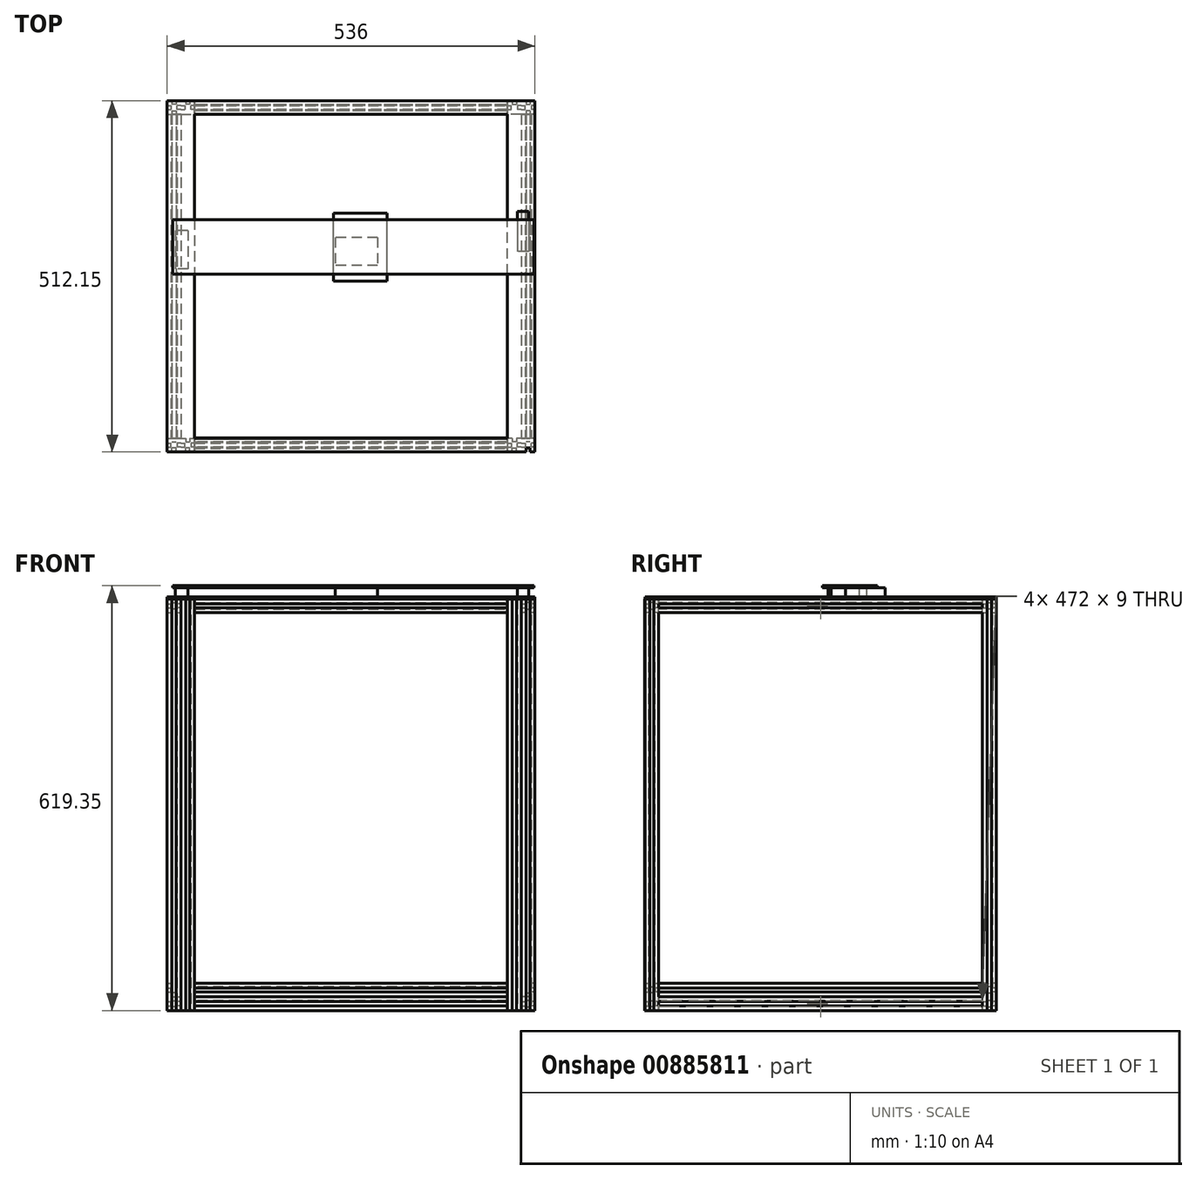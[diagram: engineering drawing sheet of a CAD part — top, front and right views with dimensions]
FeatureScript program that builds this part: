
annotation { "Feature Type Name" : "Feature", "Feature Type Description" : "" }
export const myFeature = defineFeature(function(context is Context, id is Id, definition is map)
    precondition{}
    {
        {
            var Q0;
            Q0=qCreatedBy(makeId("Right.planeOp"),FACE);
            var sketch = newSketch(context, id + "F0", { "sketchPlane" : qUnion([Q0])});
            skLineSegment(sketch, "E0.bottom", {"start": v(-73.97, 127.1) * mm, "end": v(-53.97, 127.1) * mm});
            skLineSegment(sketch, "E0.top", {"start": v(-73.97, 147.1) * mm, "end": v(-53.97, 147.1) * mm});
            skLineSegment(sketch, "E0.left", {"start": v(-73.97, 127.1) * mm, "end": v(-73.97, 147.1) * mm});
            skLineSegment(sketch, "E0.right", {"start": v(-53.97, 127.1) * mm, "end": v(-53.97, 147.1) * mm});
            skLineSegment(sketch, "E1.bottom", {"start": v(-66.97, 147.1) * mm, "end": v(-60.97, 147.1) * mm});
            skLineSegment(sketch, "E1.top", {"start": v(-66.97, 141.6) * mm, "end": v(-60.97, 141.6) * mm});
            skLineSegment(sketch, "E1.left", {"start": v(-66.97, 147.1) * mm, "end": v(-66.97, 141.6) * mm});
            skLineSegment(sketch, "E1.right", {"start": v(-60.97, 147.1) * mm, "end": v(-60.97, 141.6) * mm});
            skLineSegment(sketch, "E2.bottom", {"start": v(-53.97, 140.1) * mm, "end": v(-59.47, 140.1) * mm});
            skLineSegment(sketch, "E2.top", {"start": v(-53.97, 134.1) * mm, "end": v(-59.47, 134.1) * mm});
            skLineSegment(sketch, "E2.left", {"start": v(-53.97, 140.1) * mm, "end": v(-53.97, 134.1) * mm});
            skLineSegment(sketch, "E2.right", {"start": v(-59.47, 140.1) * mm, "end": v(-59.47, 134.1) * mm});
            skLineSegment(sketch, "E3.bottom", {"start": v(-60.97, 127.1) * mm, "end": v(-66.97, 127.1) * mm});
            skLineSegment(sketch, "E3.top", {"start": v(-60.97, 132.6) * mm, "end": v(-66.97, 132.6) * mm});
            skLineSegment(sketch, "E3.left", {"start": v(-60.97, 127.1) * mm, "end": v(-60.97, 132.6) * mm});
            skLineSegment(sketch, "E3.right", {"start": v(-66.97, 127.1) * mm, "end": v(-66.97, 132.6) * mm});
            skLineSegment(sketch, "E4.bottom", {"start": v(-73.97, 134.1) * mm, "end": v(-68.47, 134.1) * mm});
            skLineSegment(sketch, "E4.top", {"start": v(-73.97, 140.1) * mm, "end": v(-68.47, 140.1) * mm});
            skLineSegment(sketch, "E4.left", {"start": v(-73.97, 134.1) * mm, "end": v(-73.97, 140.1) * mm});
            skLineSegment(sketch, "E4.right", {"start": v(-68.47, 134.1) * mm, "end": v(-68.47, 140.1) * mm});
            skLineSegment(sketch, "E5.bottom", {"start": v(-74.01, 107.1) * mm, "end": v(-54.01, 107.1) * mm});
            skLineSegment(sketch, "E5.top", {"start": v(-74.01, 127.1) * mm, "end": v(-54.01, 127.1) * mm});
            skLineSegment(sketch, "E5.left", {"start": v(-74.01, 107.1) * mm, "end": v(-74.01, 127.1) * mm});
            skLineSegment(sketch, "E5.right", {"start": v(-54.01, 107.1) * mm, "end": v(-54.01, 127.1) * mm});
            skLineSegment(sketch, "E6.bottom", {"start": v(-67.01, 127.1) * mm, "end": v(-61.01, 127.1) * mm});
            skLineSegment(sketch, "E6.top", {"start": v(-67.01, 121.6) * mm, "end": v(-61.01, 121.6) * mm});
            skLineSegment(sketch, "E6.left", {"start": v(-67.01, 127.1) * mm, "end": v(-67.01, 121.6) * mm});
            skLineSegment(sketch, "E6.right", {"start": v(-61.01, 127.1) * mm, "end": v(-61.01, 121.6) * mm});
            skLineSegment(sketch, "E7.bottom", {"start": v(-54.01, 120.1) * mm, "end": v(-59.51, 120.1) * mm});
            skLineSegment(sketch, "E7.top", {"start": v(-54.01, 114.1) * mm, "end": v(-59.51, 114.1) * mm});
            skLineSegment(sketch, "E7.left", {"start": v(-54.01, 120.1) * mm, "end": v(-54.01, 114.1) * mm});
            skLineSegment(sketch, "E7.right", {"start": v(-59.51, 120.1) * mm, "end": v(-59.51, 114.1) * mm});
            skLineSegment(sketch, "E8.bottom", {"start": v(-61.01, 107.1) * mm, "end": v(-67.01, 107.1) * mm});
            skLineSegment(sketch, "E8.top", {"start": v(-61.01, 112.6) * mm, "end": v(-67.01, 112.6) * mm});
            skLineSegment(sketch, "E8.left", {"start": v(-61.01, 107.1) * mm, "end": v(-61.01, 112.6) * mm});
            skLineSegment(sketch, "E8.right", {"start": v(-67.01, 107.1) * mm, "end": v(-67.01, 112.6) * mm});
            skLineSegment(sketch, "E9.bottom", {"start": v(-74.01, 114.1) * mm, "end": v(-68.51, 114.1) * mm});
            skLineSegment(sketch, "E9.top", {"start": v(-74.01, 120.1) * mm, "end": v(-68.51, 120.1) * mm});
            skLineSegment(sketch, "E9.left", {"start": v(-74.01, 114.1) * mm, "end": v(-74.01, 120.1) * mm});
            skLineSegment(sketch, "E9.right", {"start": v(-68.51, 114.1) * mm, "end": v(-68.51, 120.1) * mm});
            skSolve(sketch);
        }
        {
            var Q0;
            {var subQ11=sQuery(id+"F0.wireOp",EDGE,"E0.bottom");Q0=makeQuery(id+"F0.imprint","IMPRINT",FACE,{"disambiguationData":[TD([[makeQuery(id+"F0.imprint","IMPRINT",EDGE,{"derivedFrom":subQ11}),1.0]])]});}
            var Q1;
            Q1=makeQuery(id+"F0.imprint","IMPRINT",FACE,{"disambiguationData":[TD([[makeQuery(id+"F0.imprint","IMPRINT",EDGE,{"derivedFrom":sQuery(id+"F0.wireOp",EDGE,"E6.top")}),-1.0]])]});
            extrude(context, id + "F1", {"entities" : qUnion([Q0, Q1]), "depth" : 270 * mm, "offsetDistance" : 25 * mm});
        }
        {
            var Q0;
            {var subQ0=sQuery(id+"F0.wireOp",EDGE,"E5.bottom");var subQ1=makeQuery(id+"F1.opExtrude","SWEPT_FACE",FACE,{"disambiguationData":[OSD([subQ0]),TDD([makeQuery(id+"F0.imprint","IMPRINT",EDGE,{"disambiguationData":[TD([[makeQuery(id+"F0.imprint","INTERSECT",VERTEX,{"derivedFrom":[subQ0,sQuery(id+"F0.wireOp",EDGE,"E5.left")]}),-1.0]])],"derivedFrom":subQ0})])]});Q0=makeQuery(id+"FbfQmAbu5wMZM1G_1.boolean.opBoolean","MERGE",FACE,{"derivedFrom":[subQ1,makeQuery(id+"FbfQmAbu5wMZM1G_1.opPattern","COPY",FACE,{"derivedFrom":subQ1,"instanceName":"1"})]});}
            var sketch = newSketch(context, id + "F2", { "sketchPlane" : qUnion([Q0])});
            skLineSegment(sketch, "E10.bottom", {"start": v(290, 54.12) * mm, "end": v(290, 74.12) * mm});
            skLineSegment(sketch, "E10.top", {"start": v(270, 54.12) * mm, "end": v(270, 74.12) * mm});
            skLineSegment(sketch, "E10.left", {"start": v(290, 54.12) * mm, "end": v(270, 54.12) * mm});
            skLineSegment(sketch, "E10.right", {"start": v(290, 74.12) * mm, "end": v(270, 74.12) * mm});
            skLineSegment(sketch, "E11.bottom", {"start": v(270, 61.12) * mm, "end": v(270, 67.12) * mm});
            skLineSegment(sketch, "E11.top", {"start": v(275.5, 61.12) * mm, "end": v(275.5, 67.12) * mm});
            skLineSegment(sketch, "E11.left", {"start": v(270, 61.12) * mm, "end": v(275.5, 61.12) * mm});
            skLineSegment(sketch, "E11.right", {"start": v(270, 67.12) * mm, "end": v(275.5, 67.12) * mm});
            skLineSegment(sketch, "E12.bottom", {"start": v(277, 74.12) * mm, "end": v(277, 68.62) * mm});
            skLineSegment(sketch, "E12.top", {"start": v(283, 74.12) * mm, "end": v(283, 68.62) * mm});
            skLineSegment(sketch, "E12.left", {"start": v(277, 74.12) * mm, "end": v(283, 74.12) * mm});
            skLineSegment(sketch, "E12.right", {"start": v(277, 68.62) * mm, "end": v(283, 68.62) * mm});
            skLineSegment(sketch, "E13.bottom", {"start": v(290, 67.12) * mm, "end": v(290, 61.12) * mm});
            skLineSegment(sketch, "E13.top", {"start": v(284.5, 67.12) * mm, "end": v(284.5, 61.12) * mm});
            skLineSegment(sketch, "E13.left", {"start": v(290, 67.12) * mm, "end": v(284.5, 67.12) * mm});
            skLineSegment(sketch, "E13.right", {"start": v(290, 61.12) * mm, "end": v(284.5, 61.12) * mm});
            skLineSegment(sketch, "E14.bottom", {"start": v(283, 54.12) * mm, "end": v(283, 59.62) * mm});
            skLineSegment(sketch, "E14.top", {"start": v(277, 54.12) * mm, "end": v(277, 59.62) * mm});
            skLineSegment(sketch, "E14.left", {"start": v(283, 54.12) * mm, "end": v(277, 54.12) * mm});
            skLineSegment(sketch, "E14.right", {"start": v(283, 59.62) * mm, "end": v(277, 59.62) * mm});
            skLineSegment(sketch, "E15.bottom", {"start": v(310, 54.09) * mm, "end": v(310, 74.09) * mm});
            skLineSegment(sketch, "E15.top", {"start": v(290, 54.09) * mm, "end": v(290, 74.09) * mm});
            skLineSegment(sketch, "E15.left", {"start": v(310, 54.09) * mm, "end": v(290, 54.09) * mm});
            skLineSegment(sketch, "E15.right", {"start": v(310, 74.09) * mm, "end": v(290, 74.09) * mm});
            skLineSegment(sketch, "E16.bottom", {"start": v(290, 61.09) * mm, "end": v(290, 67.09) * mm});
            skLineSegment(sketch, "E16.top", {"start": v(295.5, 61.09) * mm, "end": v(295.5, 67.09) * mm});
            skLineSegment(sketch, "E16.left", {"start": v(290, 61.09) * mm, "end": v(295.5, 61.09) * mm});
            skLineSegment(sketch, "E16.right", {"start": v(290, 67.09) * mm, "end": v(295.5, 67.09) * mm});
            skLineSegment(sketch, "E17.bottom", {"start": v(297, 74.09) * mm, "end": v(297, 68.59) * mm});
            skLineSegment(sketch, "E17.top", {"start": v(303, 74.09) * mm, "end": v(303, 68.59) * mm});
            skLineSegment(sketch, "E17.left", {"start": v(297, 74.09) * mm, "end": v(303, 74.09) * mm});
            skLineSegment(sketch, "E17.right", {"start": v(297, 68.59) * mm, "end": v(303, 68.59) * mm});
            skLineSegment(sketch, "E18.bottom", {"start": v(310, 67.09) * mm, "end": v(310, 61.09) * mm});
            skLineSegment(sketch, "E18.top", {"start": v(304.5, 67.09) * mm, "end": v(304.5, 61.09) * mm});
            skLineSegment(sketch, "E18.left", {"start": v(310, 67.09) * mm, "end": v(304.5, 67.09) * mm});
            skLineSegment(sketch, "E18.right", {"start": v(310, 61.09) * mm, "end": v(304.5, 61.09) * mm});
            skLineSegment(sketch, "E19.bottom", {"start": v(303, 54.09) * mm, "end": v(303, 59.59) * mm});
            skLineSegment(sketch, "E19.top", {"start": v(297, 54.09) * mm, "end": v(297, 59.59) * mm});
            skLineSegment(sketch, "E19.left", {"start": v(303, 54.09) * mm, "end": v(297, 54.09) * mm});
            skLineSegment(sketch, "E19.right", {"start": v(303, 59.59) * mm, "end": v(297, 59.59) * mm});
            skSolve(sketch);
        }
        {
            var Q0;
            Q0=makeQuery(id+"F2.imprint","IMPRINT",FACE,{"disambiguationData":[TD([[makeQuery(id+"F2.imprint","IMPRINT",EDGE,{"derivedFrom":sQuery(id+"F2.wireOp",EDGE,"E16.top")}),-1.0]])]});
            var Q1;
            {var subQ16=sQuery(id+"F2.wireOp",EDGE,"E10.bottom");Q1=makeQuery(id+"F2.imprint","IMPRINT",FACE,{"disambiguationData":[TD([[makeQuery(id+"F2.imprint","IMPRINT",EDGE,{"derivedFrom":subQ16}),1.0]])]});}
            extrude(context, id + "F3", {"entities" : qUnion([Q0, Q1]), "operationType" : NewBodyOperationType.ADD, "oppositeDirection" : true, "depth" : 600 * mm, "offsetDistance" : 25 * mm});
        }
        {
            var Q0;
            {var subQ1=sQuery(id+"F2.wireOp",EDGE,"E10.left");var subQ2=sQuery(id+"F2.wireOp",EDGE,"E10.top");var subQ3=makeQuery(id+"F2.imprint","INTERSECT",VERTEX,{"derivedFrom":[subQ2,subQ1]});var subQ5=sQuery(id+"F0.wireOp",EDGE,"E1.top");Q0=makeQuery(id+"F3.boolean.opBoolean","SPLIT",FACE,{"disambiguationData":[TD([makeQuery(id+"F1.opExtrude","SWEPT_FACE",FACE,{"disambiguationData":[OSD([subQ5])]})])],"derivedFrom":makeQuery(id+"F3.opExtrude","SWEPT_FACE",FACE,{"disambiguationData":[OSD([subQ2]),TDD([makeQuery(id+"F2.imprint","IMPRINT",EDGE,{"disambiguationData":[TD([[subQ3,-1.0]])],"derivedFrom":subQ2})])]})});}
            var sketch = newSketch(context, id + "F4", { "sketchPlane" : qUnion([Q0])});
            skLineSegment(sketch, "E20.bottom", {"start": v(54.16, 687.1) * mm, "end": v(74.16, 687.1) * mm});
            skLineSegment(sketch, "E20.top", {"start": v(54.16, 707.1) * mm, "end": v(74.16, 707.1) * mm});
            skLineSegment(sketch, "E20.left", {"start": v(54.16, 687.1) * mm, "end": v(54.16, 707.1) * mm});
            skLineSegment(sketch, "E20.right", {"start": v(74.16, 687.1) * mm, "end": v(74.16, 707.1) * mm});
            skLineSegment(sketch, "E21.bottom", {"start": v(61.16, 707.1) * mm, "end": v(67.16, 707.1) * mm});
            skLineSegment(sketch, "E21.top", {"start": v(61.16, 701.6) * mm, "end": v(67.16, 701.6) * mm});
            skLineSegment(sketch, "E21.left", {"start": v(61.16, 707.1) * mm, "end": v(61.16, 701.6) * mm});
            skLineSegment(sketch, "E21.right", {"start": v(67.16, 707.1) * mm, "end": v(67.16, 701.6) * mm});
            skLineSegment(sketch, "E22.bottom", {"start": v(74.16, 700.1) * mm, "end": v(68.66, 700.1) * mm});
            skLineSegment(sketch, "E22.top", {"start": v(74.16, 694.1) * mm, "end": v(68.66, 694.1) * mm});
            skLineSegment(sketch, "E22.left", {"start": v(74.16, 700.1) * mm, "end": v(74.16, 694.1) * mm});
            skLineSegment(sketch, "E22.right", {"start": v(68.66, 700.1) * mm, "end": v(68.66, 694.1) * mm});
            skLineSegment(sketch, "E23.bottom", {"start": v(67.16, 687.1) * mm, "end": v(61.16, 687.1) * mm});
            skLineSegment(sketch, "E23.top", {"start": v(67.16, 692.6) * mm, "end": v(61.16, 692.6) * mm});
            skLineSegment(sketch, "E23.left", {"start": v(67.16, 687.1) * mm, "end": v(67.16, 692.6) * mm});
            skLineSegment(sketch, "E23.right", {"start": v(61.16, 687.1) * mm, "end": v(61.16, 692.6) * mm});
            skLineSegment(sketch, "E24.bottom", {"start": v(54.16, 694.1) * mm, "end": v(59.66, 694.1) * mm});
            skLineSegment(sketch, "E24.top", {"start": v(54.16, 700.1) * mm, "end": v(59.66, 700.1) * mm});
            skLineSegment(sketch, "E24.left", {"start": v(54.16, 694.1) * mm, "end": v(54.16, 700.1) * mm});
            skLineSegment(sketch, "E24.right", {"start": v(59.66, 694.1) * mm, "end": v(59.66, 700.1) * mm});
            skLineSegment(sketch, "E25.top", {"start": v(54.12, 687.1) * mm, "end": v(74.12, 687.1) * mm});
            skLineSegment(sketch, "E26.bottom", {"start": v(61.12, 687.1) * mm, "end": v(67.12, 687.1) * mm});
            skSolve(sketch);
        }
        {
            var Q0;
            {var subQ10=sQuery(id+"F4.wireOp",EDGE,"E24.bottom");Q0=makeQuery(id+"F4.imprint","IMPRINT",FACE,{"disambiguationData":[TD([[makeQuery(id+"F4.imprint","IMPRINT",EDGE,{"derivedFrom":subQ10}),-1.0]])]});}
            var Q1;
            {var subQ20=sQuery(id+"F4.wireOp",EDGE,"E20.bottom");Q1=makeQuery(id+"F4.imprint","IMPRINT",FACE,{"disambiguationData":[TD([[makeQuery(id+"F4.imprint","IMPRINT",EDGE,{"derivedFrom":subQ20}),1.0]])]});}
            var Q2;
            {var subQ6=sQuery(id+"F4.wireOp",EDGE,"E26.top");Q2=makeQuery(id+"F4.imprint","IMPRINT",FACE,{"disambiguationData":[TD([[makeQuery(id+"F4.imprint","IMPRINT",EDGE,{"derivedFrom":subQ6}),-1.0]])]});}
            var Q3;
            {var subQ2=sQuery(id+"F4.wireOp",EDGE,"E26.left");Q3=makeQuery(id+"F4.imprint","IMPRINT",FACE,{"disambiguationData":[TD([[makeQuery(id+"F4.imprint","IMPRINT",EDGE,{"derivedFrom":subQ2}),-1.0]])]});}
            extrude(context, id + "F5", {"entities" : qUnion([Q0, Q1, Q2, Q3]), "operationType" : NewBodyOperationType.ADD, "depth" : 228 * mm, "offsetDistance" : 25 * mm});
        }
        {
            var Q0;
            {var subQ0=sQuery(id+"F2.wireOp",EDGE,"E15.left");Q0=makeQuery(id+"F3.opExtrude","SWEPT_FACE",FACE,{"disambiguationData":[OSD([subQ0]),TDD([makeQuery(id+"F2.imprint","IMPRINT",EDGE,{"disambiguationData":[TD([[makeQuery(id+"F2.imprint","INTERSECT",VERTEX,{"derivedFrom":[sQuery(id+"F2.wireOp",EDGE,"E15.bottom"),subQ0]}),-1.0]])],"derivedFrom":subQ0})])]});}
            var sketch = newSketch(context, id + "F6", { "sketchPlane" : qUnion([Q0])});
            skLineSegment(sketch, "E27.bottom", {"start": v(-309.96, 707.1) * mm, "end": v(-289.96, 707.1) * mm});
            skLineSegment(sketch, "E28.bottom", {"start": v(-296.96, 707.1) * mm, "end": v(-302.96, 707.1) * mm});
            skLineSegment(sketch, "E29.bottom", {"start": v(-310, 687.1) * mm, "end": v(-290, 687.1) * mm});
            skLineSegment(sketch, "E29.top", {"start": v(-310, 707.1) * mm, "end": v(-290, 707.1) * mm});
            skLineSegment(sketch, "E29.left", {"start": v(-310, 687.1) * mm, "end": v(-310, 707.1) * mm});
            skLineSegment(sketch, "E29.right", {"start": v(-290, 687.1) * mm, "end": v(-290, 707.1) * mm});
            skLineSegment(sketch, "E30.bottom", {"start": v(-303, 707.1) * mm, "end": v(-297, 707.1) * mm});
            skLineSegment(sketch, "E30.top", {"start": v(-303, 701.6) * mm, "end": v(-297, 701.6) * mm});
            skLineSegment(sketch, "E30.left", {"start": v(-303, 707.1) * mm, "end": v(-303, 701.6) * mm});
            skLineSegment(sketch, "E30.right", {"start": v(-297, 707.1) * mm, "end": v(-297, 701.6) * mm});
            skLineSegment(sketch, "E31.bottom", {"start": v(-290, 700.1) * mm, "end": v(-295.5, 700.1) * mm});
            skLineSegment(sketch, "E31.top", {"start": v(-290, 694.1) * mm, "end": v(-295.5, 694.1) * mm});
            skLineSegment(sketch, "E31.left", {"start": v(-290, 700.1) * mm, "end": v(-290, 694.1) * mm});
            skLineSegment(sketch, "E31.right", {"start": v(-295.5, 700.1) * mm, "end": v(-295.5, 694.1) * mm});
            skLineSegment(sketch, "E32.bottom", {"start": v(-297, 687.1) * mm, "end": v(-303, 687.1) * mm});
            skLineSegment(sketch, "E32.top", {"start": v(-297, 692.6) * mm, "end": v(-303, 692.6) * mm});
            skLineSegment(sketch, "E32.left", {"start": v(-297, 687.1) * mm, "end": v(-297, 692.6) * mm});
            skLineSegment(sketch, "E32.right", {"start": v(-303, 687.1) * mm, "end": v(-303, 692.6) * mm});
            skLineSegment(sketch, "E33.bottom", {"start": v(-310, 694.1) * mm, "end": v(-304.5, 694.1) * mm});
            skLineSegment(sketch, "E33.top", {"start": v(-310, 700.1) * mm, "end": v(-304.5, 700.1) * mm});
            skLineSegment(sketch, "E33.left", {"start": v(-310, 694.1) * mm, "end": v(-310, 700.1) * mm});
            skLineSegment(sketch, "E33.right", {"start": v(-304.5, 694.1) * mm, "end": v(-304.5, 700.1) * mm});
            skLineSegment(sketch, "E34.bottom", {"start": v(-309.96, 127.1) * mm, "end": v(-289.96, 127.1) * mm});
            skLineSegment(sketch, "E34.top", {"start": v(-309.96, 147.1) * mm, "end": v(-289.96, 147.1) * mm});
            skLineSegment(sketch, "E34.left", {"start": v(-309.96, 127.1) * mm, "end": v(-309.96, 147.1) * mm});
            skLineSegment(sketch, "E34.right", {"start": v(-289.96, 127.1) * mm, "end": v(-289.96, 147.1) * mm});
            skLineSegment(sketch, "E35.bottom", {"start": v(-302.96, 147.1) * mm, "end": v(-296.96, 147.1) * mm});
            skLineSegment(sketch, "E35.top", {"start": v(-302.96, 141.6) * mm, "end": v(-296.96, 141.6) * mm});
            skLineSegment(sketch, "E35.left", {"start": v(-302.96, 147.1) * mm, "end": v(-302.96, 141.6) * mm});
            skLineSegment(sketch, "E35.right", {"start": v(-296.96, 147.1) * mm, "end": v(-296.96, 141.6) * mm});
            skLineSegment(sketch, "E36.bottom", {"start": v(-289.96, 140.1) * mm, "end": v(-295.46, 140.1) * mm});
            skLineSegment(sketch, "E36.top", {"start": v(-289.96, 134.1) * mm, "end": v(-295.46, 134.1) * mm});
            skLineSegment(sketch, "E36.left", {"start": v(-289.96, 140.1) * mm, "end": v(-289.96, 134.1) * mm});
            skLineSegment(sketch, "E36.right", {"start": v(-295.46, 140.1) * mm, "end": v(-295.46, 134.1) * mm});
            skLineSegment(sketch, "E37.bottom", {"start": v(-296.96, 127.1) * mm, "end": v(-302.96, 127.1) * mm});
            skLineSegment(sketch, "E37.top", {"start": v(-296.96, 132.6) * mm, "end": v(-302.96, 132.6) * mm});
            skLineSegment(sketch, "E37.left", {"start": v(-296.96, 127.1) * mm, "end": v(-296.96, 132.6) * mm});
            skLineSegment(sketch, "E37.right", {"start": v(-302.96, 127.1) * mm, "end": v(-302.96, 132.6) * mm});
            skLineSegment(sketch, "E38.bottom", {"start": v(-309.96, 134.1) * mm, "end": v(-304.46, 134.1) * mm});
            skLineSegment(sketch, "E38.top", {"start": v(-309.96, 140.1) * mm, "end": v(-304.46, 140.1) * mm});
            skLineSegment(sketch, "E38.left", {"start": v(-309.96, 134.1) * mm, "end": v(-309.96, 140.1) * mm});
            skLineSegment(sketch, "E38.right", {"start": v(-304.46, 134.1) * mm, "end": v(-304.46, 140.1) * mm});
            skLineSegment(sketch, "E39.bottom", {"start": v(-310, 107.1) * mm, "end": v(-290, 107.1) * mm});
            skLineSegment(sketch, "E39.top", {"start": v(-310, 127.1) * mm, "end": v(-290, 127.1) * mm});
            skLineSegment(sketch, "E39.left", {"start": v(-310, 107.1) * mm, "end": v(-310, 127.1) * mm});
            skLineSegment(sketch, "E39.right", {"start": v(-290, 107.1) * mm, "end": v(-290, 127.1) * mm});
            skLineSegment(sketch, "E40.bottom", {"start": v(-303, 127.1) * mm, "end": v(-297, 127.1) * mm});
            skLineSegment(sketch, "E40.top", {"start": v(-303, 121.6) * mm, "end": v(-297, 121.6) * mm});
            skLineSegment(sketch, "E40.left", {"start": v(-303, 127.1) * mm, "end": v(-303, 121.6) * mm});
            skLineSegment(sketch, "E40.right", {"start": v(-297, 127.1) * mm, "end": v(-297, 121.6) * mm});
            skLineSegment(sketch, "E41.bottom", {"start": v(-290, 120.1) * mm, "end": v(-295.5, 120.1) * mm});
            skLineSegment(sketch, "E41.top", {"start": v(-290, 114.1) * mm, "end": v(-295.5, 114.1) * mm});
            skLineSegment(sketch, "E41.left", {"start": v(-290, 120.1) * mm, "end": v(-290, 114.1) * mm});
            skLineSegment(sketch, "E41.right", {"start": v(-295.5, 120.1) * mm, "end": v(-295.5, 114.1) * mm});
            skLineSegment(sketch, "E42.bottom", {"start": v(-297, 107.1) * mm, "end": v(-303, 107.1) * mm});
            skLineSegment(sketch, "E42.top", {"start": v(-297, 112.6) * mm, "end": v(-303, 112.6) * mm});
            skLineSegment(sketch, "E42.left", {"start": v(-297, 107.1) * mm, "end": v(-297, 112.6) * mm});
            skLineSegment(sketch, "E42.right", {"start": v(-303, 107.1) * mm, "end": v(-303, 112.6) * mm});
            skLineSegment(sketch, "E43.bottom", {"start": v(-310, 114.1) * mm, "end": v(-304.5, 114.1) * mm});
            skLineSegment(sketch, "E43.top", {"start": v(-310, 120.1) * mm, "end": v(-304.5, 120.1) * mm});
            skLineSegment(sketch, "E43.left", {"start": v(-310, 114.1) * mm, "end": v(-310, 120.1) * mm});
            skLineSegment(sketch, "E43.right", {"start": v(-304.5, 114.1) * mm, "end": v(-304.5, 120.1) * mm});
            skSolve(sketch);
        }
        {
            var Q0;
            {var subQ13=sQuery(id+"F6.wireOp",EDGE,"E34.bottom");Q0=makeQuery(id+"F6.imprint","IMPRINT",FACE,{"disambiguationData":[TD([[makeQuery(id+"F6.imprint","IMPRINT",EDGE,{"derivedFrom":subQ13}),1.0]])]});}
            var Q1;
            {var subQ5=sQuery(id+"F6.wireOp",EDGE,"E38.bottom");Q1=makeQuery(id+"F6.imprint","IMPRINT",FACE,{"disambiguationData":[TD([[makeQuery(id+"F6.imprint","IMPRINT",EDGE,{"derivedFrom":subQ5}),-1.0]])]});}
            var Q2;
            {var subQ2=sQuery(id+"F6.wireOp",EDGE,"E40.left");Q2=makeQuery(id+"F6.imprint","IMPRINT",FACE,{"disambiguationData":[TD([[makeQuery(id+"F6.imprint","IMPRINT",EDGE,{"derivedFrom":subQ2}),-1.0]])]});}
            var Q3;
            {var subQ6=sQuery(id+"F6.wireOp",EDGE,"E40.top");Q3=makeQuery(id+"F6.imprint","IMPRINT",FACE,{"disambiguationData":[TD([[makeQuery(id+"F6.imprint","IMPRINT",EDGE,{"derivedFrom":subQ6}),-1.0]])]});}
            var Q4;
            {var subQ12=sQuery(id+"F6.wireOp",EDGE,"9667445b-14a2-414e-8e40-848a2c53a070.bottom");Q4=makeQuery(id+"F6.imprint","IMPRINT",FACE,{"disambiguationData":[TD([[makeQuery(id+"F6.imprint","IMPRINT",EDGE,{"derivedFrom":subQ12}),-1.0]])]});}
            var Q5;
            {var subQ13=sQuery(id+"F6.wireOp",EDGE,"E27.bottom");Q5=makeQuery(id+"F6.imprint","IMPRINT",FACE,{"disambiguationData":[TD([[makeQuery(id+"F6.imprint","IMPRINT",EDGE,{"derivedFrom":subQ13}),1.0]])]});}
            var Q6;
            {var subQ6=sQuery(id+"F6.wireOp",EDGE,"E30.top");Q6=makeQuery(id+"F6.imprint","IMPRINT",FACE,{"disambiguationData":[TD([[makeQuery(id+"F6.imprint","IMPRINT",EDGE,{"derivedFrom":subQ6}),-1.0]])]});}
            var Q7;
            {var subQ2=sQuery(id+"F6.wireOp",EDGE,"E30.left");Q7=makeQuery(id+"F6.imprint","IMPRINT",FACE,{"disambiguationData":[TD([[makeQuery(id+"F6.imprint","IMPRINT",EDGE,{"derivedFrom":subQ2}),-1.0]])]});}
            extrude(context, id + "F7", {"entities" : qUnion([Q0, Q1, Q2, Q3, Q4, Q5, Q6, Q7]), "operationType" : NewBodyOperationType.ADD, "depth" : 236 * mm, "offsetDistance" : 25 * mm});
        }
        {
            var Q0;
            Q0=makeQuery(id+"F1.opExtrude","SWEPT_BODY",BODY,{"disambiguationData":[OSD([sQuery(id+"F0.wireOp",EDGE,"E0.bottom"),sQuery(id+"F0.wireOp",EDGE,"E0.top"),sQuery(id+"F0.wireOp",EDGE,"E0.left"),sQuery(id+"F0.wireOp",EDGE,"E0.right"),sQuery(id+"F0.wireOp",EDGE,"E1.top"),sQuery(id+"F0.wireOp",EDGE,"E1.left"),sQuery(id+"F0.wireOp",EDGE,"E1.right"),sQuery(id+"F0.wireOp",EDGE,"E2.bottom"),sQuery(id+"F0.wireOp",EDGE,"E2.top"),sQuery(id+"F0.wireOp",EDGE,"E2.right"),sQuery(id+"F0.wireOp",EDGE,"E3.top"),sQuery(id+"F0.wireOp",EDGE,"E3.left"),sQuery(id+"F0.wireOp",EDGE,"E3.right"),sQuery(id+"F0.wireOp",EDGE,"E4.bottom"),sQuery(id+"F0.wireOp",EDGE,"E4.top"),sQuery(id+"F0.wireOp",EDGE,"E4.right"),sQuery(id+"F0.wireOp",EDGE,"E5.bottom"),sQuery(id+"F0.wireOp",EDGE,"E5.top"),sQuery(id+"F0.wireOp",EDGE,"E5.left"),sQuery(id+"F0.wireOp",EDGE,"E5.right"),sQuery(id+"F0.wireOp",EDGE,"E6.bottom"),sQuery(id+"F0.wireOp",EDGE,"E6.top"),sQuery(id+"F0.wireOp",EDGE,"E6.left"),sQuery(id+"F0.wireOp",EDGE,"E6.right"),sQuery(id+"F0.wireOp",EDGE,"E7.bottom"),sQuery(id+"F0.wireOp",EDGE,"E7.top"),sQuery(id+"F0.wireOp",EDGE,"E7.right"),sQuery(id+"F0.wireOp",EDGE,"E8.top"),sQuery(id+"F0.wireOp",EDGE,"E8.left"),sQuery(id+"F0.wireOp",EDGE,"E8.right"),sQuery(id+"F0.wireOp",EDGE,"E9.bottom"),sQuery(id+"F0.wireOp",EDGE,"E9.top"),sQuery(id+"F0.wireOp",EDGE,"E9.right")])]});
            var Q1;
            Q1=makeQuery(id+"F7.opExtrude","CAP_FACE",FACE,{"disambiguationData":[OSD([sQuery(id+"F6.wireOp",EDGE,"E27.bottom"),sQuery(id+"F6.wireOp",EDGE,"E27.top"),sQuery(id+"F6.wireOp",EDGE,"E27.left"),sQuery(id+"F6.wireOp",EDGE,"E27.right"),sQuery(id+"F6.wireOp",EDGE,"697817fb-edbd-40a5-a29d-952f93a9c78b.top"),sQuery(id+"F6.wireOp",EDGE,"697817fb-edbd-40a5-a29d-952f93a9c78b.left"),sQuery(id+"F6.wireOp",EDGE,"697817fb-edbd-40a5-a29d-952f93a9c78b.right"),sQuery(id+"F6.wireOp",EDGE,"15fd4d5f-bd60-4fe3-bdb7-a61c8bb0770d.bottom"),sQuery(id+"F6.wireOp",EDGE,"15fd4d5f-bd60-4fe3-bdb7-a61c8bb0770d.top"),sQuery(id+"F6.wireOp",EDGE,"15fd4d5f-bd60-4fe3-bdb7-a61c8bb0770d.right"),sQuery(id+"F6.wireOp",EDGE,"E28.top"),sQuery(id+"F6.wireOp",EDGE,"E28.left"),sQuery(id+"F6.wireOp",EDGE,"E28.right"),sQuery(id+"F6.wireOp",EDGE,"9667445b-14a2-414e-8e40-848a2c53a070.bottom"),sQuery(id+"F6.wireOp",EDGE,"9667445b-14a2-414e-8e40-848a2c53a070.top"),sQuery(id+"F6.wireOp",EDGE,"9667445b-14a2-414e-8e40-848a2c53a070.right"),sQuery(id+"F6.wireOp",EDGE,"E29.bottom"),sQuery(id+"F6.wireOp",EDGE,"E29.top"),sQuery(id+"F6.wireOp",EDGE,"E29.left"),sQuery(id+"F6.wireOp",EDGE,"E29.right"),sQuery(id+"F6.wireOp",EDGE,"E30.bottom"),sQuery(id+"F6.wireOp",EDGE,"E30.top"),sQuery(id+"F6.wireOp",EDGE,"E30.left"),sQuery(id+"F6.wireOp",EDGE,"E30.right"),sQuery(id+"F6.wireOp",EDGE,"E31.bottom"),sQuery(id+"F6.wireOp",EDGE,"E31.top"),sQuery(id+"F6.wireOp",EDGE,"E31.right"),sQuery(id+"F6.wireOp",EDGE,"E32.top"),sQuery(id+"F6.wireOp",EDGE,"E32.left"),sQuery(id+"F6.wireOp",EDGE,"E32.right"),sQuery(id+"F6.wireOp",EDGE,"E33.bottom"),sQuery(id+"F6.wireOp",EDGE,"E33.top"),sQuery(id+"F6.wireOp",EDGE,"E33.right")])],"isStart":false});
            mirror(context, id + "F8", {"operationType" : NewBodyOperationType.ADD, "entities" : qUnion([Q0]), "mirrorPlane" : qUnion([Q1])});
        }
        {
            var Q0;
            Q0=makeQuery(id+"F1.opExtrude","SWEPT_BODY",BODY,{"disambiguationData":[OSD([sQuery(id+"F0.wireOp",EDGE,"E0.bottom"),sQuery(id+"F0.wireOp",EDGE,"E0.top"),sQuery(id+"F0.wireOp",EDGE,"E0.left"),sQuery(id+"F0.wireOp",EDGE,"E0.right"),sQuery(id+"F0.wireOp",EDGE,"E1.top"),sQuery(id+"F0.wireOp",EDGE,"E1.left"),sQuery(id+"F0.wireOp",EDGE,"E1.right"),sQuery(id+"F0.wireOp",EDGE,"E2.bottom"),sQuery(id+"F0.wireOp",EDGE,"E2.top"),sQuery(id+"F0.wireOp",EDGE,"E2.right"),sQuery(id+"F0.wireOp",EDGE,"E3.top"),sQuery(id+"F0.wireOp",EDGE,"E3.left"),sQuery(id+"F0.wireOp",EDGE,"E3.right"),sQuery(id+"F0.wireOp",EDGE,"E4.bottom"),sQuery(id+"F0.wireOp",EDGE,"E4.top"),sQuery(id+"F0.wireOp",EDGE,"E4.right"),sQuery(id+"F0.wireOp",EDGE,"E5.bottom"),sQuery(id+"F0.wireOp",EDGE,"E5.top"),sQuery(id+"F0.wireOp",EDGE,"E5.left"),sQuery(id+"F0.wireOp",EDGE,"E5.right"),sQuery(id+"F0.wireOp",EDGE,"E6.bottom"),sQuery(id+"F0.wireOp",EDGE,"E6.top"),sQuery(id+"F0.wireOp",EDGE,"E6.left"),sQuery(id+"F0.wireOp",EDGE,"E6.right"),sQuery(id+"F0.wireOp",EDGE,"E7.bottom"),sQuery(id+"F0.wireOp",EDGE,"E7.top"),sQuery(id+"F0.wireOp",EDGE,"E7.right"),sQuery(id+"F0.wireOp",EDGE,"E8.top"),sQuery(id+"F0.wireOp",EDGE,"E8.left"),sQuery(id+"F0.wireOp",EDGE,"E8.right"),sQuery(id+"F0.wireOp",EDGE,"E9.bottom"),sQuery(id+"F0.wireOp",EDGE,"E9.top"),sQuery(id+"F0.wireOp",EDGE,"E9.right")])]});
            var Q1;
            Q1=makeQuery(id+"F8.opPattern","COPY",FACE,{"derivedFrom":makeQuery(id+"F5.opExtrude","CAP_FACE",FACE,{"disambiguationData":[OSD([sQuery(id+"F4.wireOp",EDGE,"E20.bottom"),sQuery(id+"F4.wireOp",EDGE,"E20.top"),sQuery(id+"F4.wireOp",EDGE,"E20.left"),sQuery(id+"F4.wireOp",EDGE,"E20.right"),sQuery(id+"F4.wireOp",EDGE,"E21.top"),sQuery(id+"F4.wireOp",EDGE,"E21.left"),sQuery(id+"F4.wireOp",EDGE,"E21.right"),sQuery(id+"F4.wireOp",EDGE,"E22.bottom"),sQuery(id+"F4.wireOp",EDGE,"E22.top"),sQuery(id+"F4.wireOp",EDGE,"E22.right"),sQuery(id+"F4.wireOp",EDGE,"E23.top"),sQuery(id+"F4.wireOp",EDGE,"E23.left"),sQuery(id+"F4.wireOp",EDGE,"E23.right"),sQuery(id+"F4.wireOp",EDGE,"E24.bottom"),sQuery(id+"F4.wireOp",EDGE,"E24.top"),sQuery(id+"F4.wireOp",EDGE,"E24.right"),sQuery(id+"F4.wireOp",EDGE,"E25.bottom"),sQuery(id+"F4.wireOp",EDGE,"E25.top"),sQuery(id+"F4.wireOp",EDGE,"E25.left"),sQuery(id+"F4.wireOp",EDGE,"E25.right"),sQuery(id+"F4.wireOp",EDGE,"E26.bottom"),sQuery(id+"F4.wireOp",EDGE,"E26.top"),sQuery(id+"F4.wireOp",EDGE,"E26.left"),sQuery(id+"F4.wireOp",EDGE,"E26.right"),sQuery(id+"F4.wireOp",EDGE,"5deab17a-8b40-4d6d-9c5f-e36e1ba74caf.bottom"),sQuery(id+"F4.wireOp",EDGE,"5deab17a-8b40-4d6d-9c5f-e36e1ba74caf.top"),sQuery(id+"F4.wireOp",EDGE,"5deab17a-8b40-4d6d-9c5f-e36e1ba74caf.right"),sQuery(id+"F4.wireOp",EDGE,"d7008ef7-543d-4fc7-9499-e6056a1d5e29.top"),sQuery(id+"F4.wireOp",EDGE,"d7008ef7-543d-4fc7-9499-e6056a1d5e29.left"),sQuery(id+"F4.wireOp",EDGE,"d7008ef7-543d-4fc7-9499-e6056a1d5e29.right"),sQuery(id+"F4.wireOp",EDGE,"5877a9cc-45be-4406-93d5-3bf86a8e6dfc.bottom"),sQuery(id+"F4.wireOp",EDGE,"5877a9cc-45be-4406-93d5-3bf86a8e6dfc.top"),sQuery(id+"F4.wireOp",EDGE,"5877a9cc-45be-4406-93d5-3bf86a8e6dfc.right")])],"isStart":false}),"instanceName":"1"});
            mirror(context, id + "F9", {"operationType" : NewBodyOperationType.ADD, "entities" : qUnion([Q0]), "mirrorPlane" : qUnion([Q1])});
        }
        {
            var Q0;
            Q0=makeQuery(id+"F9.opPattern","COPY",FACE,{"derivedFrom":makeQuery(id+"F8.opPattern","COPY",FACE,{"derivedFrom":makeQuery(id+"F3.opExtrude","SWEPT_FACE",FACE,{"disambiguationData":[OSD([sQuery(id+"F2.wireOp",EDGE,"E14.right")])]}),"instanceName":"1"}),"instanceName":"1"});
            var Q1;
            Q1=makeQuery(id+"F8.opPattern","COPY",FACE,{"derivedFrom":makeQuery(id+"F3.opExtrude","SWEPT_FACE",FACE,{"disambiguationData":[OSD([sQuery(id+"F2.wireOp",EDGE,"E14.right")])]}),"instanceName":"1"});
            extrude(context, id + "F10", {"entities" : qUnion([Q0, Q1]), "operationType" : NewBodyOperationType.ADD, "depth" : 5.5 * mm, "offsetDistance" : 25 * mm});
        }
        {
            var Q0;
            {var subQ0=sQuery(id+"F2.wireOp",EDGE,"E14.right");var subQ1=makeQuery(id+"F8.opPattern","COPY",EDGE,{"derivedFrom":makeQuery(id+"F3.opExtrude","CAP_EDGE",EDGE,{"disambiguationData":[OSD([subQ0])],"isStart":false}),"instanceName":"1"});var subQ2=sQuery(id+"F6.wireOp",EDGE,"E29.top");var subQ4=sQuery(id+"F4.wireOp",EDGE,"E20.top");var subQ5=sQuery(id+"F4.wireOp",EDGE,"E21.bottom");var subQ6=sQuery(id+"F2.wireOp",EDGE,"E11.left");var subQ7=sQuery(id+"F2.wireOp",EDGE,"E10.left");var subQ8=sQuery(id+"F2.wireOp",EDGE,"E10.top");var subQ9=makeQuery(id+"F3.opExtrude","CAP_FACE",FACE,{"disambiguationData":[OSD([sQuery(id+"F2.wireOp",EDGE,"E10.bottom"),subQ8,subQ7,sQuery(id+"F2.wireOp",EDGE,"E10.right"),sQuery(id+"F2.wireOp",EDGE,"E11.top"),subQ6,sQuery(id+"F2.wireOp",EDGE,"E11.right"),sQuery(id+"F2.wireOp",EDGE,"E12.bottom"),sQuery(id+"F2.wireOp",EDGE,"E12.top"),sQuery(id+"F2.wireOp",EDGE,"E12.right"),sQuery(id+"F2.wireOp",EDGE,"E13.top"),sQuery(id+"F2.wireOp",EDGE,"E13.left"),sQuery(id+"F2.wireOp",EDGE,"E13.right"),sQuery(id+"F2.wireOp",EDGE,"E14.bottom"),sQuery(id+"F2.wireOp",EDGE,"E14.top"),subQ0,sQuery(id+"F2.wireOp",EDGE,"E15.bottom"),sQuery(id+"F2.wireOp",EDGE,"E15.top"),sQuery(id+"F2.wireOp",EDGE,"E15.left"),sQuery(id+"F2.wireOp",EDGE,"E15.right"),sQuery(id+"F2.wireOp",EDGE,"E16.bottom"),sQuery(id+"F2.wireOp",EDGE,"E16.top"),sQuery(id+"F2.wireOp",EDGE,"E16.left"),sQuery(id+"F2.wireOp",EDGE,"E16.right"),sQuery(id+"F2.wireOp",EDGE,"E17.bottom"),sQuery(id+"F2.wireOp",EDGE,"E17.top"),sQuery(id+"F2.wireOp",EDGE,"E17.right"),sQuery(id+"F2.wireOp",EDGE,"E18.top"),sQuery(id+"F2.wireOp",EDGE,"E18.left"),sQuery(id+"F2.wireOp",EDGE,"E18.right"),sQuery(id+"F2.wireOp",EDGE,"E19.bottom"),sQuery(id+"F2.wireOp",EDGE,"E19.top"),sQuery(id+"F2.wireOp",EDGE,"E19.right")])],"isStart":false});var subQ12=makeQuery(id+"F2.imprint","IMPRINT",EDGE,{"disambiguationData":[TD([[makeQuery(id+"F2.imprint","INTERSECT",VERTEX,{"derivedFrom":[subQ8,subQ7]}),-1.0]])],"derivedFrom":subQ8});var subQ16=makeQuery(id+"F7.boolean.opBoolean","MERGE",FACE,{"derivedFrom":[makeQuery(id+"F5.boolean.opBoolean","MERGE",FACE,{"derivedFrom":[subQ9,makeQuery(id+"F5.opExtrude","SWEPT_FACE",FACE,{"disambiguationData":[OSD([subQ4]),TDD([makeQuery(id+"F4.imprint","IMPRINT",EDGE,{"disambiguationData":[TD([[makeQuery(id+"F4.imprint","INTERSECT",VERTEX,{"derivedFrom":[makeQuery(id+"F3.opExtrude","CAP_EDGE",EDGE,{"disambiguationData":[OSD([subQ8]),TDD([subQ12])],"isStart":false}),subQ4,sQuery(id+"F4.wireOp",EDGE,"E20.left")]}),-1.0]])],"derivedFrom":subQ4}),makeQuery(id+"F4.imprint","IMPRINT",EDGE,{"disambiguationData":[TD([[makeQuery(id+"F4.imprint","INTERSECT",VERTEX,{"derivedFrom":[subQ4,subQ5,sQuery(id+"F4.wireOp",EDGE,"E21.left")]}),1.0]])],"derivedFrom":subQ4})])]}),makeQuery(id+"F5.opExtrude","SWEPT_FACE",FACE,{"disambiguationData":[OSD([subQ4]),TDD([makeQuery(id+"F4.imprint","IMPRINT",EDGE,{"disambiguationData":[TD([[makeQuery(id+"F4.imprint","INTERSECT",VERTEX,{"derivedFrom":[subQ4,sQuery(id+"F4.wireOp",EDGE,"E20.right")]}),1.0]])],"derivedFrom":subQ4})])]})]}),makeQuery(id+"F7.opExtrude","SWEPT_FACE",FACE,{"disambiguationData":[OSD([subQ2]),TDD([makeQuery(id+"F6.imprint","IMPRINT",EDGE,{"disambiguationData":[TD([[makeQuery(id+"F6.imprint","INTERSECT",VERTEX,{"derivedFrom":[subQ2,sQuery(id+"F6.wireOp",EDGE,"E29.left")]}),-1.0]])],"derivedFrom":subQ2})])]}),makeQuery(id+"F7.opExtrude","SWEPT_FACE",FACE,{"disambiguationData":[OSD([subQ2]),TDD([makeQuery(id+"F6.imprint","IMPRINT",EDGE,{"disambiguationData":[TD([[makeQuery(id+"F6.imprint","INTERSECT",VERTEX,{"derivedFrom":[subQ2,sQuery(id+"F6.wireOp",EDGE,"E29.right")]}),1.0]])],"derivedFrom":subQ2})])]})]});var subQ17=makeQuery(id+"F8.boolean.opBoolean","MERGE",FACE,{"derivedFrom":[subQ16,makeQuery(id+"F8.opPattern","COPY",FACE,{"derivedFrom":subQ16,"instanceName":"1"})]});Q0=makeQuery(id+"F10.boolean.opBoolean","MERGE",FACE,{"derivedFrom":[makeQuery(id+"F9.boolean.opBoolean","MERGE",FACE,{"derivedFrom":[subQ17,makeQuery(id+"F9.opPattern","COPY",FACE,{"derivedFrom":subQ17,"instanceName":"1"})]}),makeQuery(id+"F10.opExtrude","SWEPT_FACE",FACE,{"disambiguationData":[OSD([subQ0]),TDD([subQ1])]}),makeQuery(id+"F10.opExtrude","SWEPT_FACE",FACE,{"disambiguationData":[OSD([subQ0]),TDD([makeQuery(id+"F9.opPattern","COPY",EDGE,{"derivedFrom":subQ1,"instanceName":"1"})])]})]});}
            var sketch = newSketch(context, id + "F11", { "sketchPlane" : qUnion([Q0])});
            skLineSegment(sketch, "E44.bottom", {"start": v(-226, 437.91) * mm, "end": v(310, 437.91) * mm});
            skLineSegment(sketch, "E44.top", {"start": v(-226, -74.09) * mm, "end": v(310, -74.09) * mm});
            skLineSegment(sketch, "E44.left", {"start": v(-226, 437.91) * mm, "end": v(-226, -74.09) * mm});
            skLineSegment(sketch, "E44.right", {"start": v(310, 437.91) * mm, "end": v(310, -74.09) * mm});
            skLineSegment(sketch, "E45.bottom", {"start": v(-186, 418) * mm, "end": v(270, 418) * mm});
            skLineSegment(sketch, "E45.top", {"start": v(-186, -54.12) * mm, "end": v(270, -54.12) * mm});
            skLineSegment(sketch, "E45.left", {"start": v(-186, 418) * mm, "end": v(-186, -54.12) * mm});
            skLineSegment(sketch, "E45.right", {"start": v(270, 418) * mm, "end": v(270, -54.12) * mm});
            skSolve(sketch);
        }
        {
            var Q0;
            {var subQ0=makeQuery(id+"F3.opExtrude","CAP_EDGE",EDGE,{"disambiguationData":[OSD([sQuery(id+"F2.wireOp",EDGE,"E19.right")])],"isStart":false});Q0=makeQuery(id+"F11.imprint","IMPRINT",FACE,{"disambiguationData":[TD([[makeQuery(id+"F11.imprint","IMPRINT",EDGE,{"derivedFrom":makeQuery(id+"F9.opPattern","COPY",EDGE,{"derivedFrom":subQ0,"instanceName":"1"})}),1.0]])]});}
            var Q1;
            {var subQ4=sQuery(id+"F2.wireOp",EDGE,"E11.top");var subQ5=makeQuery(id+"F8.opPattern","COPY",EDGE,{"derivedFrom":makeQuery(id+"F3.opExtrude","CAP_EDGE",EDGE,{"disambiguationData":[OSD([subQ4])],"isStart":false}),"instanceName":"1"});Q1=makeQuery(id+"F11.imprint","IMPRINT",FACE,{"disambiguationData":[TD([[makeQuery(id+"F11.imprint","IMPRINT",EDGE,{"derivedFrom":subQ5}),1.0]])]});}
            var Q2;
            {var subQ0=makeQuery(id+"F3.opExtrude","CAP_EDGE",EDGE,{"disambiguationData":[OSD([sQuery(id+"F2.wireOp",EDGE,"E19.right")])],"isStart":false});Q2=makeQuery(id+"F11.imprint","IMPRINT",FACE,{"disambiguationData":[TD([[makeQuery(id+"F11.imprint","IMPRINT",EDGE,{"derivedFrom":subQ0}),-1.0]])]});}
            var Q3;
            {var subQ3=sQuery(id+"F2.wireOp",EDGE,"E11.top");var subQ22=makeQuery(id+"F3.opExtrude","CAP_EDGE",EDGE,{"disambiguationData":[OSD([subQ3])],"isStart":false});Q3=makeQuery(id+"F11.imprint","IMPRINT",FACE,{"disambiguationData":[TD([[makeQuery(id+"F11.imprint","IMPRINT",EDGE,{"derivedFrom":subQ22}),-1.0]])]});}
            var Q4;
            Q4=makeQuery(id+"F11.imprint","IMPRINT",FACE,{"disambiguationData":[TD([[makeQuery(id+"F11.imprint","IMPRINT",EDGE,{"derivedFrom":makeQuery(id+"F3.opExtrude","CAP_EDGE",EDGE,{"disambiguationData":[OSD([sQuery(id+"F2.wireOp",EDGE,"E13.top")])],"isStart":false})}),-1.0]])]});
            var Q5;
            Q5=makeQuery(id+"F11.imprint","IMPRINT",FACE,{"disambiguationData":[TD([[makeQuery(id+"F11.imprint","IMPRINT",EDGE,{"derivedFrom":makeQuery(id+"F3.opExtrude","CAP_EDGE",EDGE,{"disambiguationData":[OSD([sQuery(id+"F2.wireOp",EDGE,"E18.top")])],"isStart":false})}),-1.0]])]});
            var Q6;
            {var subQ143=sQuery(id+"F11.wireOp",EDGE,"E45.bottom");Q6=makeQuery(id+"F11.imprint","IMPRINT",FACE,{"disambiguationData":[TD([[makeQuery(id+"F11.imprint","IMPRINT",EDGE,{"derivedFrom":subQ143}),1.0]])]});}
            var Q7;
            {var subQ5=makeQuery(id+"F3.opExtrude","CAP_EDGE",EDGE,{"disambiguationData":[OSD([sQuery(id+"F2.wireOp",EDGE,"E12.right")])],"isStart":false});Q7=makeQuery(id+"F11.imprint","IMPRINT",FACE,{"disambiguationData":[TD([[makeQuery(id+"F11.imprint","IMPRINT",EDGE,{"derivedFrom":subQ5}),-1.0]])]});}
            var Q8;
            {var subQ0=sQuery(id+"F2.wireOp",EDGE,"E14.bottom");Q8=makeQuery(id+"F11.imprint","IMPRINT",FACE,{"disambiguationData":[TD([[makeQuery(id+"F11.imprint","IMPRINT",EDGE,{"derivedFrom":makeQuery(id+"F3.opExtrude","CAP_EDGE",EDGE,{"disambiguationData":[OSD([subQ0])],"isStart":false})}),-1.0]])]});}
            var Q9;
            Q9=makeQuery(id+"F11.imprint","IMPRINT",FACE,{"disambiguationData":[TD([[makeQuery(id+"F11.imprint","IMPRINT",EDGE,{"derivedFrom":makeQuery(id+"F8.opPattern","COPY",EDGE,{"derivedFrom":makeQuery(id+"F3.opExtrude","CAP_EDGE",EDGE,{"disambiguationData":[OSD([sQuery(id+"F2.wireOp",EDGE,"E13.top")])],"isStart":false}),"instanceName":"1"})}),1.0]])]});
            var Q10;
            Q10=makeQuery(id+"F11.imprint","IMPRINT",FACE,{"disambiguationData":[TD([[makeQuery(id+"F11.imprint","IMPRINT",EDGE,{"derivedFrom":makeQuery(id+"F8.opPattern","COPY",EDGE,{"derivedFrom":makeQuery(id+"F3.opExtrude","CAP_EDGE",EDGE,{"disambiguationData":[OSD([sQuery(id+"F2.wireOp",EDGE,"E18.top")])],"isStart":false}),"instanceName":"1"})}),1.0]])]});
            var Q11;
            {var subQ1=makeQuery(id+"F8.opPattern","COPY",EDGE,{"derivedFrom":makeQuery(id+"F3.opExtrude","CAP_EDGE",EDGE,{"disambiguationData":[OSD([sQuery(id+"F2.wireOp",EDGE,"E17.bottom")])],"isStart":false}),"instanceName":"1"});Q11=makeQuery(id+"F11.imprint","IMPRINT",FACE,{"disambiguationData":[TD([[makeQuery(id+"F11.imprint","IMPRINT",EDGE,{"derivedFrom":subQ1}),1.0]])]});}
            var Q12;
            {var subQ5=makeQuery(id+"F8.opPattern","COPY",EDGE,{"derivedFrom":makeQuery(id+"F3.opExtrude","CAP_EDGE",EDGE,{"disambiguationData":[OSD([sQuery(id+"F2.wireOp",EDGE,"E12.right")])],"isStart":false}),"instanceName":"1"});Q12=makeQuery(id+"F11.imprint","IMPRINT",FACE,{"disambiguationData":[TD([[makeQuery(id+"F11.imprint","IMPRINT",EDGE,{"derivedFrom":subQ5}),1.0]])]});}
            var Q13;
            {var subQ5=makeQuery(id+"F9.opPattern","COPY",EDGE,{"derivedFrom":makeQuery(id+"F8.opPattern","COPY",EDGE,{"derivedFrom":makeQuery(id+"F3.opExtrude","CAP_EDGE",EDGE,{"disambiguationData":[OSD([sQuery(id+"F2.wireOp",EDGE,"E12.right")])],"isStart":false}),"instanceName":"1"}),"instanceName":"1"});Q13=makeQuery(id+"F11.imprint","IMPRINT",FACE,{"disambiguationData":[TD([[makeQuery(id+"F11.imprint","IMPRINT",EDGE,{"derivedFrom":subQ5}),-1.0]])]});}
            var Q14;
            {var subQ1=makeQuery(id+"F9.opPattern","COPY",EDGE,{"derivedFrom":makeQuery(id+"F8.opPattern","COPY",EDGE,{"derivedFrom":makeQuery(id+"F3.opExtrude","CAP_EDGE",EDGE,{"disambiguationData":[OSD([sQuery(id+"F2.wireOp",EDGE,"E17.bottom")])],"isStart":false}),"instanceName":"1"}),"instanceName":"1"});Q14=makeQuery(id+"F11.imprint","IMPRINT",FACE,{"disambiguationData":[TD([[makeQuery(id+"F11.imprint","IMPRINT",EDGE,{"derivedFrom":subQ1}),-1.0]])]});}
            var Q15;
            Q15=makeQuery(id+"F11.imprint","IMPRINT",FACE,{"disambiguationData":[TD([[makeQuery(id+"F11.imprint","IMPRINT",EDGE,{"derivedFrom":makeQuery(id+"F9.opPattern","COPY",EDGE,{"derivedFrom":makeQuery(id+"F8.opPattern","COPY",EDGE,{"derivedFrom":makeQuery(id+"F3.opExtrude","CAP_EDGE",EDGE,{"disambiguationData":[OSD([sQuery(id+"F2.wireOp",EDGE,"E18.top")])],"isStart":false}),"instanceName":"1"}),"instanceName":"1"})}),-1.0]])]});
            var Q16;
            Q16=makeQuery(id+"F11.imprint","IMPRINT",FACE,{"disambiguationData":[TD([[makeQuery(id+"F11.imprint","IMPRINT",EDGE,{"derivedFrom":makeQuery(id+"F9.opPattern","COPY",EDGE,{"derivedFrom":makeQuery(id+"F8.opPattern","COPY",EDGE,{"derivedFrom":makeQuery(id+"F3.opExtrude","CAP_EDGE",EDGE,{"disambiguationData":[OSD([sQuery(id+"F2.wireOp",EDGE,"E13.top")])],"isStart":false}),"instanceName":"1"}),"instanceName":"1"})}),-1.0]])]});
            var Q17;
            {var subQ4=sQuery(id+"F2.wireOp",EDGE,"E14.bottom");Q17=makeQuery(id+"F11.imprint","IMPRINT",FACE,{"disambiguationData":[TD([[makeQuery(id+"F11.imprint","IMPRINT",EDGE,{"derivedFrom":makeQuery(id+"F9.opPattern","COPY",EDGE,{"derivedFrom":makeQuery(id+"F3.opExtrude","CAP_EDGE",EDGE,{"disambiguationData":[OSD([subQ4])],"isStart":false}),"instanceName":"1"})}),1.0]])]});}
            var Q18;
            Q18=makeQuery(id+"F11.imprint","IMPRINT",FACE,{"disambiguationData":[TD([[makeQuery(id+"F11.imprint","IMPRINT",EDGE,{"derivedFrom":makeQuery(id+"F9.opPattern","COPY",EDGE,{"derivedFrom":makeQuery(id+"F3.opExtrude","CAP_EDGE",EDGE,{"disambiguationData":[OSD([sQuery(id+"F2.wireOp",EDGE,"E13.top")])],"isStart":false}),"instanceName":"1"})}),1.0]])]});
            var Q19;
            Q19=makeQuery(id+"F11.imprint","IMPRINT",FACE,{"disambiguationData":[TD([[makeQuery(id+"F11.imprint","IMPRINT",EDGE,{"derivedFrom":makeQuery(id+"F9.opPattern","COPY",EDGE,{"derivedFrom":makeQuery(id+"F3.opExtrude","CAP_EDGE",EDGE,{"disambiguationData":[OSD([sQuery(id+"F2.wireOp",EDGE,"E18.top")])],"isStart":false}),"instanceName":"1"})}),1.0]])]});
            var Q20;
            {var subQ1=makeQuery(id+"F9.opPattern","COPY",EDGE,{"derivedFrom":makeQuery(id+"F3.opExtrude","CAP_EDGE",EDGE,{"disambiguationData":[OSD([sQuery(id+"F2.wireOp",EDGE,"E17.bottom")])],"isStart":false}),"instanceName":"1"});Q20=makeQuery(id+"F11.imprint","IMPRINT",FACE,{"disambiguationData":[TD([[makeQuery(id+"F11.imprint","IMPRINT",EDGE,{"derivedFrom":subQ1}),1.0]])]});}
            var Q21;
            {var subQ5=makeQuery(id+"F9.opPattern","COPY",EDGE,{"derivedFrom":makeQuery(id+"F3.opExtrude","CAP_EDGE",EDGE,{"disambiguationData":[OSD([sQuery(id+"F2.wireOp",EDGE,"E12.right")])],"isStart":false}),"instanceName":"1"});Q21=makeQuery(id+"F11.imprint","IMPRINT",FACE,{"disambiguationData":[TD([[makeQuery(id+"F11.imprint","IMPRINT",EDGE,{"derivedFrom":subQ5}),1.0]])]});}
            extrude(context, id + "F12", {"entities" : qUnion([Q0, Q1, Q2, Q3, Q4, Q5, Q6, Q7, Q8, Q9, Q10, Q11, Q12, Q13, Q14, Q15, Q16, Q17, Q18, Q19, Q20, Q21]), "depth" : 3.17 * mm, "offsetDistance" : 25 * mm});
        }
        {
            var Q0;
            Q0=makeQuery(id+"F12.opExtrude","CAP_FACE",FACE,{"disambiguationData":[OSD([sQuery(id+"F2.wireOp",EDGE,"E10.top"),sQuery(id+"F2.wireOp",EDGE,"E17.bottom"),sQuery(id+"F2.wireOp",EDGE,"E17.top"),sQuery(id+"F2.wireOp",EDGE,"E17.right"),sQuery(id+"F4.wireOp",EDGE,"E20.top"),sQuery(id+"F4.wireOp",EDGE,"E20.left"),sQuery(id+"F11.wireOp",EDGE,"E44.bottom"),sQuery(id+"F11.wireOp",EDGE,"E44.top"),sQuery(id+"F11.wireOp",EDGE,"E44.left"),sQuery(id+"F11.wireOp",EDGE,"E44.right"),sQuery(id+"F11.wireOp",EDGE,"E45.bottom"),sQuery(id+"F11.wireOp",EDGE,"E45.left"),sQuery(id+"F11.wireOp",EDGE,"E45.right")])],"isStart":false});
            var sketch = newSketch(context, id + "F13", { "sketchPlane" : qUnion([Q0])});
            skLineSegment(sketch, "E46.bottom", {"start": v(-195.56, 248.74) * mm, "end": v(-214.46, 248.74) * mm});
            skLineSegment(sketch, "E46.top", {"start": v(-195.56, 192.77) * mm, "end": v(-214.46, 192.77) * mm});
            skLineSegment(sketch, "E46.left", {"start": v(-195.56, 248.74) * mm, "end": v(-195.56, 192.77) * mm});
            skLineSegment(sketch, "E46.right", {"start": v(-214.46, 248.74) * mm, "end": v(-214.46, 192.77) * mm});
            skLineSegment(sketch, "E47.bottom", {"start": v(300.72, 276.25) * mm, "end": v(284.23, 276.25) * mm});
            skLineSegment(sketch, "E47.top", {"start": v(300.72, 218) * mm, "end": v(284.23, 218) * mm});
            skLineSegment(sketch, "E47.left", {"start": v(300.72, 276.25) * mm, "end": v(300.72, 218) * mm});
            skLineSegment(sketch, "E47.right", {"start": v(284.23, 276.25) * mm, "end": v(284.23, 218) * mm});
            skSolve(sketch);
        }
        {
            var Q0;
            Q0=makeQuery(id+"F13.imprint","IMPRINT",FACE,{"disambiguationData":[TD([[makeQuery(id+"F13.imprint","IMPRINT",EDGE,{"derivedFrom":sQuery(id+"F13.wireOp",EDGE,"E47.bottom")}),1.0]])]});
            var Q1;
            Q1=makeQuery(id+"F13.imprint","IMPRINT",FACE,{"disambiguationData":[TD([[makeQuery(id+"F13.imprint","IMPRINT",EDGE,{"derivedFrom":sQuery(id+"F13.wireOp",EDGE,"E46.bottom")}),1.0]])]});
            extrude(context, id + "F14", {"entities" : qUnion([Q0, Q1]), "depth" : 13 * mm, "offsetDistance" : 25 * mm});
        }
        {
            var Q0;
            Q0=makeQuery(id+"F14.opExtrude","CAP_FACE",FACE,{"disambiguationData":[OSD([sQuery(id+"F13.wireOp",EDGE,"E46.bottom"),sQuery(id+"F13.wireOp",EDGE,"E46.top"),sQuery(id+"F13.wireOp",EDGE,"E46.left"),sQuery(id+"F13.wireOp",EDGE,"E46.right")])],"isStart":false});
            var sketch = newSketch(context, id + "F15", { "sketchPlane" : qUnion([Q0])});
            skLineSegment(sketch, "E48.bottom", {"start": v(-217.73, 264.5) * mm, "end": v(308.12, 264.5) * mm});
            skLineSegment(sketch, "E48.top", {"start": v(-217.73, 184.76) * mm, "end": v(308.12, 184.76) * mm});
            skLineSegment(sketch, "E48.left", {"start": v(-217.73, 264.5) * mm, "end": v(-217.73, 184.76) * mm});
            skLineSegment(sketch, "E48.right", {"start": v(308.12, 264.5) * mm, "end": v(308.12, 184.76) * mm});
            skSolve(sketch);
        }
        {
            var Q0;
            Q0=makeQuery(id+"F15.imprint","IMPRINT",FACE,{"disambiguationData":[TD([[makeQuery(id+"F15.imprint","IMPRINT",EDGE,{"derivedFrom":makeQuery(id+"F14.opExtrude","CAP_EDGE",EDGE,{"disambiguationData":[OSD([sQuery(id+"F13.wireOp",EDGE,"E46.bottom")])],"isStart":false})}),1.0]])]});
            var Q1;
            Q1=makeQuery(id+"F15.imprint","IMPRINT",FACE,{"disambiguationData":[TD([[makeQuery(id+"F15.imprint","IMPRINT",EDGE,{"derivedFrom":sQuery(id+"F15.wireOp",EDGE,"E48.bottom")}),-1.0]])]});
            extrude(context, id + "F16", {"entities" : qUnion([Q0, Q1]), "depth" : 3.17 * mm, "offsetDistance" : 25 * mm});
        }
        {
            var Q0;
            Q0=makeQuery(id+"F16.opExtrude","CAP_FACE",FACE,{"disambiguationData":[OSD([sQuery(id+"F15.wireOp",EDGE,"E48.bottom"),sQuery(id+"F15.wireOp",EDGE,"E48.top"),sQuery(id+"F15.wireOp",EDGE,"E48.left"),sQuery(id+"F15.wireOp",EDGE,"E48.right")])],"isStart":true});
            var sketch = newSketch(context, id + "F17", { "sketchPlane" : qUnion([Q0])});
            skLineSegment(sketch, "E49.bottom", {"start": v(80.7, -238.65) * mm, "end": v(19.17, -238.65) * mm});
            skLineSegment(sketch, "E49.top", {"start": v(80.7, -197.48) * mm, "end": v(19.17, -197.48) * mm});
            skLineSegment(sketch, "E49.left", {"start": v(80.7, -238.65) * mm, "end": v(80.7, -197.48) * mm});
            skLineSegment(sketch, "E49.right", {"start": v(19.17, -238.65) * mm, "end": v(19.17, -197.48) * mm});
            skSolve(sketch);
        }
        {
            var Q0;
            Q0=makeQuery(id+"F17.imprint","IMPRINT",FACE,{"disambiguationData":[TD([[makeQuery(id+"F17.imprint","IMPRINT",EDGE,{"derivedFrom":sQuery(id+"F17.wireOp",EDGE,"E49.bottom")}),-1.0]])]});
            extrude(context, id + "F18", {"entities" : qUnion([Q0]), "depth" : 13 * mm, "offsetDistance" : 25 * mm});
        }
        {
            var Q0;
            Q0=makeQuery(id+"F18.opExtrude","CAP_FACE",FACE,{"disambiguationData":[OSD([sQuery(id+"F17.wireOp",EDGE,"E49.bottom"),sQuery(id+"F17.wireOp",EDGE,"E49.top"),sQuery(id+"F17.wireOp",EDGE,"E49.left"),sQuery(id+"F17.wireOp",EDGE,"E49.right")])],"isStart":false});
            var sketch = newSketch(context, id + "F19", { "sketchPlane" : qUnion([Q0])});
            skLineSegment(sketch, "E50.bottom", {"start": v(16.1, -174.7) * mm, "end": v(94.37, -174.7) * mm});
            skLineSegment(sketch, "E50.top", {"start": v(16.1, -274.01) * mm, "end": v(94.37, -274.01) * mm});
            skLineSegment(sketch, "E50.left", {"start": v(16.1, -174.7) * mm, "end": v(16.1, -274.01) * mm});
            skLineSegment(sketch, "E50.right", {"start": v(94.37, -174.7) * mm, "end": v(94.37, -274.01) * mm});
            skSolve(sketch);
        }
        {
            var Q0;
            Q0=makeQuery(id+"F19.imprint","IMPRINT",FACE,{"disambiguationData":[TD([[makeQuery(id+"F19.imprint","IMPRINT",EDGE,{"derivedFrom":sQuery(id+"F19.wireOp",EDGE,"E50.bottom")}),-1.0]])]});
            var Q1;
            Q1=makeQuery(id+"F19.imprint","IMPRINT",FACE,{"disambiguationData":[TD([[makeQuery(id+"F19.imprint","IMPRINT",EDGE,{"derivedFrom":makeQuery(id+"F18.opExtrude","CAP_EDGE",EDGE,{"disambiguationData":[OSD([sQuery(id+"F17.wireOp",EDGE,"E49.bottom")])],"isStart":false})}),-1.0]])]});
            extrude(context, id + "F20", {"entities" : qUnion([Q0, Q1]), "operationType" : NewBodyOperationType.ADD, "depth" : 3.17 * mm, "offsetDistance" : 25 * mm});
        }
    });
